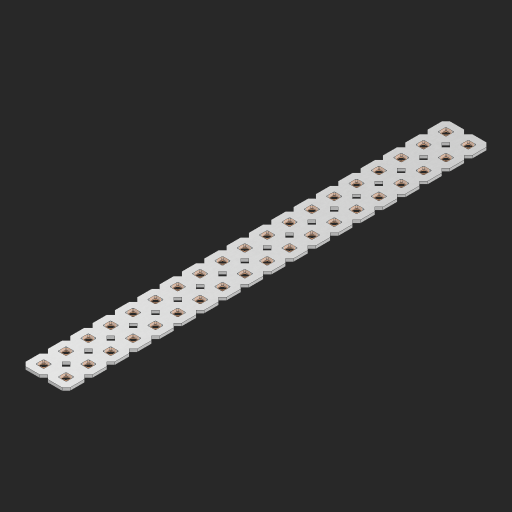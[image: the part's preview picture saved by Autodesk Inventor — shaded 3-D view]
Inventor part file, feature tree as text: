
AUTODESK INVENTOR PART (.ipt)
format: ipt  version: 2023 (Build 270158000, 158)  size: 710,144 bytes
history: native  units: in
note: dims shown in document units (in); Inventor stores cm internally (conversion verified against a paired STEP export)
features: other x39, extrude x37, sketch x2, pattern_linear x1
ambient origin geometry x8: Origin, YZ Plane, XZ Plane, XY Plane, X Axis, Y Axis, Z Axis, Center Point
bodies: Solid1 (feature_tree), Body (feature_tree)
feature tree (79):
  pattern_linear  "Rectangular Pattern1"  Spacing1=0.09in  [1 undecoded]
  sketch  "Sketch1"  dims[d1=0.5in]
  sketch  "Sketch2"  dims[d2=0.182in d3=0.09in d4=0.09in d5=0.09in d6=0.09in d7=0.09in d8=0.09in d9=0.09in d10=0.09in d11=0.02in d13=0.0in d14=0.172in d15=0.0625in d16=0.0in d19=0.5in d22=0.5in]
  other  "Srf1"
  other  "Srf126"
  other  "Srf127"
  other  "Srf128"
  other  "Srf129"
  other  "Srf130"
  other  "Srf131"
  other  "Srf250"
  other  "Srf251"
  other  "Srf252"
  other  "Srf253"
  other  "Srf254"
  other  "Srf255"
  other  "Srf256"
  other  "Srf257"
  other  "Srf258"
  other  "Srf259"
  other  "Srf260"
  other  "Srf261"
  other  "Srf268"
  other  "Srf269"
  other  "Srf270"
  other  "Srf271"
  other  "Srf272"
  other  "Srf273"
  other  "Srf274"
  other  "Srf275"
  other  "Srf276"
  other  "Srf277"
  other  "Srf278"
  other  "Srf279"
  other  "Srf280"
  other  "Srf281"
  other  "Srf282"
  other  "Srf283"
  other  "Srf284"
  other  "Srf285"
  other  "Srf286"
  other  "Circle"
  extrude  "ExtrusionSrf126"  Depth=0.09in
  extrude  "ExtrusionSrf127"  Depth=0.09in
  extrude  "ExtrusionSrf128"  Depth=0.09in
  extrude  "ExtrusionSrf129"  Depth=0.09in
  extrude  "ExtrusionSrf130"  Depth=0.09in
  extrude  "ExtrusionSrf131"  Depth=0.09in
  extrude  "ExtrusionSrf250"  Depth=0.09in
  extrude  "ExtrusionSrf251"  Depth=0.02in
  extrude  "ExtrusionSrf252"  TaperAngle=0.0deg  [1 undecoded]
  extrude  "ExtrusionSrf253"  Depth=0.5in
  extrude  "ExtrusionSrf254"  Depth=0.0625in TaperAngle=0.0deg
  extrude  "ExtrusionSrf255"  Depth=0.5in
  extrude  "ExtrusionSrf256"  Depth=0.5in
  extrude  "ExtrusionSrf257"  [1 undecoded]
  extrude  "ExtrusionSrf258"  [1 undecoded]
  extrude  "ExtrusionSrf259"  [1 undecoded]
  extrude  "ExtrusionSrf260"  [1 undecoded]
  extrude  "ExtrusionSrf261"  [1 undecoded]
  extrude  "ExtrusionSrf268"  [1 undecoded]
  extrude  "ExtrusionSrf269"  [1 undecoded]
  extrude  "ExtrusionSrf270"  [1 undecoded]
  extrude  "ExtrusionSrf271"  [1 undecoded]
  extrude  "ExtrusionSrf272"  [1 undecoded]
  extrude  "ExtrusionSrf273"  [1 undecoded]
  extrude  "ExtrusionSrf274"  [1 undecoded]
  extrude  "ExtrusionSrf275"  [1 undecoded]
  extrude  "ExtrusionSrf276"  [1 undecoded]
  extrude  "ExtrusionSrf277"  [1 undecoded]
  extrude  "ExtrusionSrf278"  [1 undecoded]
  extrude  "ExtrusionSrf279"  [1 undecoded]
  extrude  "ExtrusionSrf280"  [1 undecoded]
  extrude  "ExtrusionSrf281"  [1 undecoded]
  extrude  "ExtrusionSrf282"  [1 undecoded]
  extrude  "ExtrusionSrf283"  [1 undecoded]
  extrude  "ExtrusionSrf284"  [1 undecoded]
  extrude  "ExtrusionSrf285"  [1 undecoded]
  extrude  "ExtrusionSrf286"  [1 undecoded]
note: 26 required parameter values undecoded (feature->parameter linkage not recoverable at this tier; creation-order binding heuristic only, values carry confidence <= 0.55)
